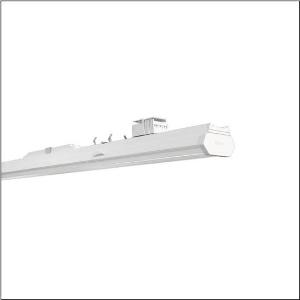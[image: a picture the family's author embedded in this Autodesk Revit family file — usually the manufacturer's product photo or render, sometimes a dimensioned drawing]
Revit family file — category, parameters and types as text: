
# Revit family: licross_11_protected_mo_51tp11dn495g
name_source: partatom
category: Lighting Fixtures
units: mm (PartAtom-declared; Revit-internal decimal feet)

## family parameters
Cut with Voids When Loaded = No
Host = Face
Light Source = No
Part Type = Normal
Room Calculation Point = No
Round Connector Dimension = Use Diameter
Shared = No

## types (1)
- --- (1 x LED, 9930 lm, 57.1 W, 4000K)
    Apparent Load = 57 VA
    CIE Flux Codes = 83 94 98 100 100
    Color Rendering = 80
    Color Temperature = 4000K
    Default Elevation = 1800 mm
    Description = Licross 11 Protected MO, luminaire insert, of sheet steel, galvanised, coil coated, white, length: 1.500mm, width: 90mm, height: 101mm, LED rated luminous flux: 9.980lm, light colour: 840, SDCM (Standard Deviation of Colour Matching)MacAdam ≤ 2 SDCM (initial), control gear: DALI 2, with plug, 5-pole, with phase selection, mains connection: 220..240V, AC, 50/60Hz, rated input power: 57W, internal wiring halogen-free, primary light control with lens, of plastic, primary optical cover: cover, of PMMA, light emission: direct distribution, primary light characteristic: symmetric, protection rating (complete): IP64, insulation class (complete): insulation class I (protective earthing), certification: CE, ENEC, VDE, UKCA, protection symbol: D if used in an environment with conductive dust loads with corresponding accessories, impact resistance: IK06, permissible ambient temperature for indoor applications: -25..+35°C, corresponds to IFS (International Featured Standards) requirements for safety and quality in the food industry, reducing of maximum allowable ambient temperature of 5°C with ceiling mounting, LABS conformity tested according to VDMA 24364:2018-05, The light source and the operating device comply with the requirements of the Ecodesign Regulation (EU) 2019/2020 and are replaceable in accordance with this regulation, packaging unit: 1 piece
    Height = 92 mm
    Lamp = 1 x LED
    Lamp Light Flux = 9930 lm
    Lamp Power = 57.1 W
    Lamp count = 1
    Length = 1500 mm
    Luminous efficacy = 174 lm/W
    Manufacturer = Siteco
    ModVariant = No
    Model = 51TP11DN495G
    Mounting Place = Ceiling
    Mounting Type = Pendant
    Number of Poles = 1
    OnlyDefault = Yes
    Power Factor = 1
    Product Name = Licross 11 Protected MO
    Product group = luminaire insert | ceiling pendant
    ProductGroupID = 901
    Protection Class = Protection class I
    Protection Degree = IP 64
    RLX_Detail_Level = 1
    RLX_Emergency_Light_Flux = 0 lm
    RLX_Emergency_Type = 0
    RLX_Emergency_Type_DB = No
    RlxData = <blob elided: 24369 chars, md5=47fa0a0d>
    Socket = socket
    Standby Power = 0 W
    System Light Flux = 9930 lm
    System Power = 57 W
    Type Comments = factory setting: luminous flux: 100 % | dim-lin: 254 | 378 mA
    Type Image = l_1256148.jpg
    URL = http://relux.com
    VarID = @adj_104071
    Voltage = 0 V
    Weight = 0.00 kg
    Width = 88 mm

## geometry (parser evidence)
native form markers: Blend x4, Sweep x10
no freeform markers — native parametric forms only
